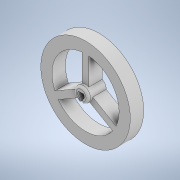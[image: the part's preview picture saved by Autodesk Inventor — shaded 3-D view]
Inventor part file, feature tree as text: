
AUTODESK INVENTOR PART (.ipt)
format: ipt  version: 2020 (Build 240168000, 168)  size: 162,816 bytes
history: native  units: mm
features: extrude x3, sketch x3, other x1, fillet x1
ambient origin geometry x8: Origin, YZ Plane, XZ Plane, XY Plane, X Axis, Y Axis, Z Axis, Center Point
bodies: Body1 (feature_tree)
feature tree (8):
  other  "Твердое тело1"
  extrude  "Выдавливание1"  Depth=40.0mm
  extrude  "Выдавливание2"  Depth=30.0mm
  extrude  "Выдавливание3"  Depth=6.5mm
  fillet  "Сопряжение1"  Radius=3.0mm
  sketch  "Эскиз1"
  sketch  "Эскиз2"
  sketch  "Эскиз3"
